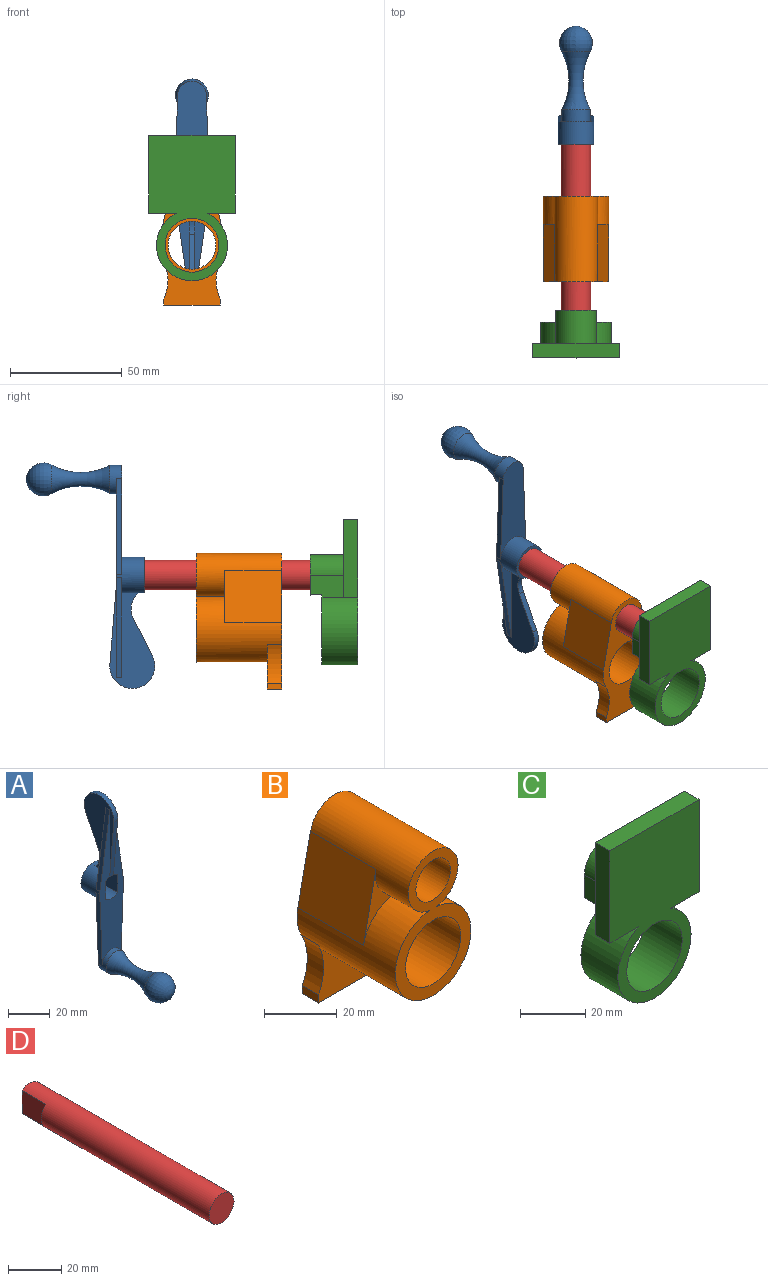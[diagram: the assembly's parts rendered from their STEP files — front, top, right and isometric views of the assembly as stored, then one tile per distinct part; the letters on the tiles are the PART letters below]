
ASSEMBLY  parts=4 mates=3
PART A: 26 faces, bbox 23.8x52.2x105.2 mm
  f0: plane 44.54x6.64mm, normal (0,1,0), area 115.7mm2, adj f5,f6,f17
  f1: plane 44.54x6.64mm, normal (0,1,0), area 115.7mm2, adj f6,f10,f16
  f2: cylinder r=6.61mm len=12.7mm, axis (0,1,0), area 109.1mm2, adj f3,f11,f12,f14
  f3: plane 12.7x10.53mm, normal (1,0,0), area 133.7mm2, adj f2,f4,f12,f14
  f4: cylinder r=6.61mm len=12.7mm, axis (0,1,0), area 80.6mm2, adj f3,f11,f12,f14,f15,f16,f17
  f5: plane 44.54x6.64mm, normal (-0.99,0,0.15), area 114.4mm2, adj f0,f6,f12,f17
  f6: cylinder r=8mm len=16mm, axis (0,1,0), area 499.6mm2, adj f0,f1,f5,f7,f9,f10,f12,f13
  f7: plane 42.61x2.54mm, normal (-1,0,-0.04), area 108.3mm2, adj f6,f8,f12,f13
  f8: cylinder r=6.33mm len=12.67mm, axis (0,1,0), area 160.5mm2, adj f7,f9,f12,f13,f24
  f9: plane 42.61x2.54mm, normal (1,0,-0.04), area 108.3mm2, adj f6,f8,f12,f13
  f10: plane 44.54x6.64mm, normal (0.99,0,0.15), area 114.4mm2, adj f1,f6,f12,f16
  f11: plane 12.7x10.53mm, normal (-1,0,0), area 133.7mm2, adj f2,f4,f12,f14
  f12: plane 88.64x16mm, normal (0,-1,0), area 778.6mm2, adj f2,f3,f4,f5,f6,f7,f8,f9
  f13: plane 48.69x15.99mm, normal (0,1,0), area 574.6mm2, adj f6,f7,f8,f9
  f14: plane 16x16mm, normal (0,1,0), area 102.2mm2, adj f2,f3,f4,f6,f11
  f15: plane 2.54x0.14mm, normal (0,0.74,0.67), area 0.4mm2, adj f4,f16,f17,f23
  f16: plane 44.21x20.07mm, normal (1,0,0), area 473.1mm2, adj f1,f4,f6,f10,f12,f15,f18,f19
  f17: plane 44.21x20.07mm, normal (-1,0,0), area 473.1mm2, adj f0,f4,f5,f6,f12,f15,f18,f19
  f18: plane 2.54x0.84mm, normal (0,0.74,0.67), area 2.7mm2, adj f6,f16,f17,f19
  f19: cylinder r=9.47mm len=10.68mm, axis (-1,0,0), area 29.1mm2, adj f16,f17,f18,f20
  f20: plane 16.69x8.45mm, normal (0,0.89,-0.45), area 47.5mm2, adj f16,f17,f19,f21
  f21: cylinder r=10.03mm len=20.07mm, axis (-1,0,0), area 94.1mm2, adj f16,f17,f20,f22
  f22: plane 33.35x2.76mm, normal (0,-1,-0.08), area 85mm2, adj f16,f17,f21,f23
  f23: plane 11.28x2.54mm, normal (0,0,-1), area 28.6mm2, adj f15,f16,f17,f22
  f24: torus R=30.29mm, axis (0,-1,0), area 711.4mm2, adj f8,f25
  f25: revolved ~12.83x6.41mm, area 0mm2, adj f24
PART B: 16 faces, bbox 29.3x38.1x60.5 mm
  f0: cylinder r=14.67mm len=38.1mm, axis (0,1,0), area 2263.6mm2, adj f1,f4,f5,f6,f7,f8,f9,f10
  f1: cylinder r=9.67mm len=38.1mm, axis (0,1,0), area 1408.7mm2, adj f0,f4,f5,f6,f7,f8,f9
  f2: cylinder r=10.67mm len=38.1mm, axis (0,1,0), area 2553.8mm2, adj f4,f5
  f3: cylinder r=6.67mm len=38.1mm, axis (0,1,0), area 1596.1mm2, adj f4,f5
  f4: plane 48.54x29.34mm, normal (0,-1,0), area 472.2mm2, adj f0,f1,f2,f3
  f5: plane 60.54x29.34mm, normal (0,1,0), area 902.9mm2, adj f0,f1,f2,f3,f7,f9,f10,f11
  f6: plane 23.17x13.09mm, normal (0,-1,0), area 58.5mm2, adj f0,f1,f7
  f7: plane 25.4x23.17mm, normal (-0.98,0,0.21), area 601.4mm2, adj f0,f1,f5,f6
  f8: plane 23.17x13.09mm, normal (0,-1,0), area 58.5mm2, adj f0,f1,f9
  f9: plane 25.4x23.17mm, normal (0.98,0,0.21), area 601.4mm2, adj f0,f1,f5,f8
  f10: cylinder r=18.43mm len=17.04mm, axis (0,1,0), area 112.5mm2, adj f0,f5,f11,f15
  f11: plane 6.35x2.67mm, normal (-1,0,0), area 16.9mm2, adj f5,f10,f12,f15
  f12: plane 25.34x6.35mm, normal (0,0,-1), area 160.9mm2, adj f5,f11,f13,f15
  f13: plane 6.35x2.67mm, normal (1,0,0), area 16.9mm2, adj f5,f12,f14,f15
  f14: cylinder r=18.43mm len=17.04mm, axis (0,1,0), area 112.5mm2, adj f0,f5,f13,f15
  f15: plane 25.82x19.7mm, normal (0,-1,0), area 313.8mm2, adj f0,f10,f11,f12,f13,f14
PART C: 19 faces, bbox 38.7x21.3x64.9 mm
  f0: plane 16x12.52mm, normal (0,0,-1), area 100.7mm2, adj f2,f4,f6,f8,f9,f10
  f1: plane 18.02x18.02mm, normal (0,1,0), area 194.1mm2, adj f10,f11,f12,f13,f14,f17,f18
  f2: plane 38.67x34.67mm, normal (0,1,0), area 1035.6mm2, adj f0,f6,f7,f10,f11,f15,f16,f17
  f3: plane 10.67x10.67mm, normal (0,1,0), area 89.4mm2, adj f12
  f4: cylinder r=15.87mm len=31.74mm, axis (0,-1,0), area 1370.4mm2, adj f0,f8,f9,f15
  f5: cylinder r=12mm len=24mm, axis (0,-1,0), area 1206.7mm2, adj f8,f9
  f6: plane 34.67x6.35mm, normal (1,0,0), area 220.2mm2, adj f0,f2,f7,f8
  f7: plane 38.67x6.35mm, normal (0,0,1), area 245.6mm2, adj f2,f6,f8,f16
  f8: plane 64.88x38.67mm, normal (0,-1,0), area 1665.6mm2, adj f0,f4,f5,f6,f7,f15,f16
  f9: plane 31.74x31.5mm, normal (0,1,0), area 346.5mm2, adj f0,f4,f5,f10,f13,f14,f15,f17
  f10: plane 14.99x9.87mm, normal (1,0,0), area 140.9mm2, adj f0,f1,f2,f9,f11,f14
  f11: cylinder r=9.01mm len=18.02mm, axis (0,-1,0), area 424.1mm2, adj f1,f2,f10,f17
  f12: cylinder r=5.33mm len=14.99mm, axis (0,-1,0), area 502.2mm2, adj f1,f3
  f13: cylinder r=9.01mm len=5.54mm, axis (0,-1,0), area 30mm2, adj f1,f9,f14,f18
  f14: plane 6.24x5.33mm, normal (0,0,-1), area 33.3mm2, adj f1,f9,f10,f13
  f15: plane 16x12.52mm, normal (0,0,-1), area 100.7mm2, adj f2,f4,f8,f9,f16,f17
  f16: plane 34.67x6.35mm, normal (-1,0,0), area 220.2mm2, adj f2,f7,f8,f15
  f17: plane 14.99x9.87mm, normal (-1,0,0), area 140.9mm2, adj f1,f2,f9,f11,f15,f18
  f18: plane 6.24x5.33mm, normal (0,0,-1), area 33.3mm2, adj f1,f9,f13,f17
PART D: 7 faces, bbox 13.2x101.6x13.2 mm
  f0: plane 13.22x8mm, normal (0,1,0), area 98.9mm2, adj f1,f3,f5
  f1: cylinder r=6.61mm len=101.6mm, axis (0,1,0), area 3910.7mm2, adj f0,f2,f3,f4,f5,f6
  f2: plane 13.22x13.22mm, normal (0,-1,0), area 137.3mm2, adj f1
  f3: plane 12.7x10.53mm, normal (-1,0,0), area 133.7mm2, adj f0,f1,f4
  f4: plane 10.53x2.61mm, normal (0,1,0), area 19.2mm2, adj f1,f3
  f5: plane 12.7x10.53mm, normal (1,0,0), area 133.7mm2, adj f0,f1,f6
  f6: plane 10.53x2.61mm, normal (0,1,0), area 19.2mm2, adj f1,f5
PLACE A rot(axis=(1,0,0),180deg) t=(-58.8,105.41,74.54)mm
PLACE B rot(axis=(0,0,1),180deg) t=(-36.13,34.04,-30.14)mm
PLACE C t=(197.14,0,-15.87)mm
PLACE D t=(-6.67,107.95,17.53)mm
MATE fastened A.f2 <-> D.f1  axis (0,-1,0) through (0,107.95,24.2)mm
MATE fastened C.f11 <-> D.f1  axis (0,1,0) through (0,6.35,24.2)mm
MATE fastened B.f1 <-> C.f11  axis (0,-1,0) through (0,34.04,24.2)mm
